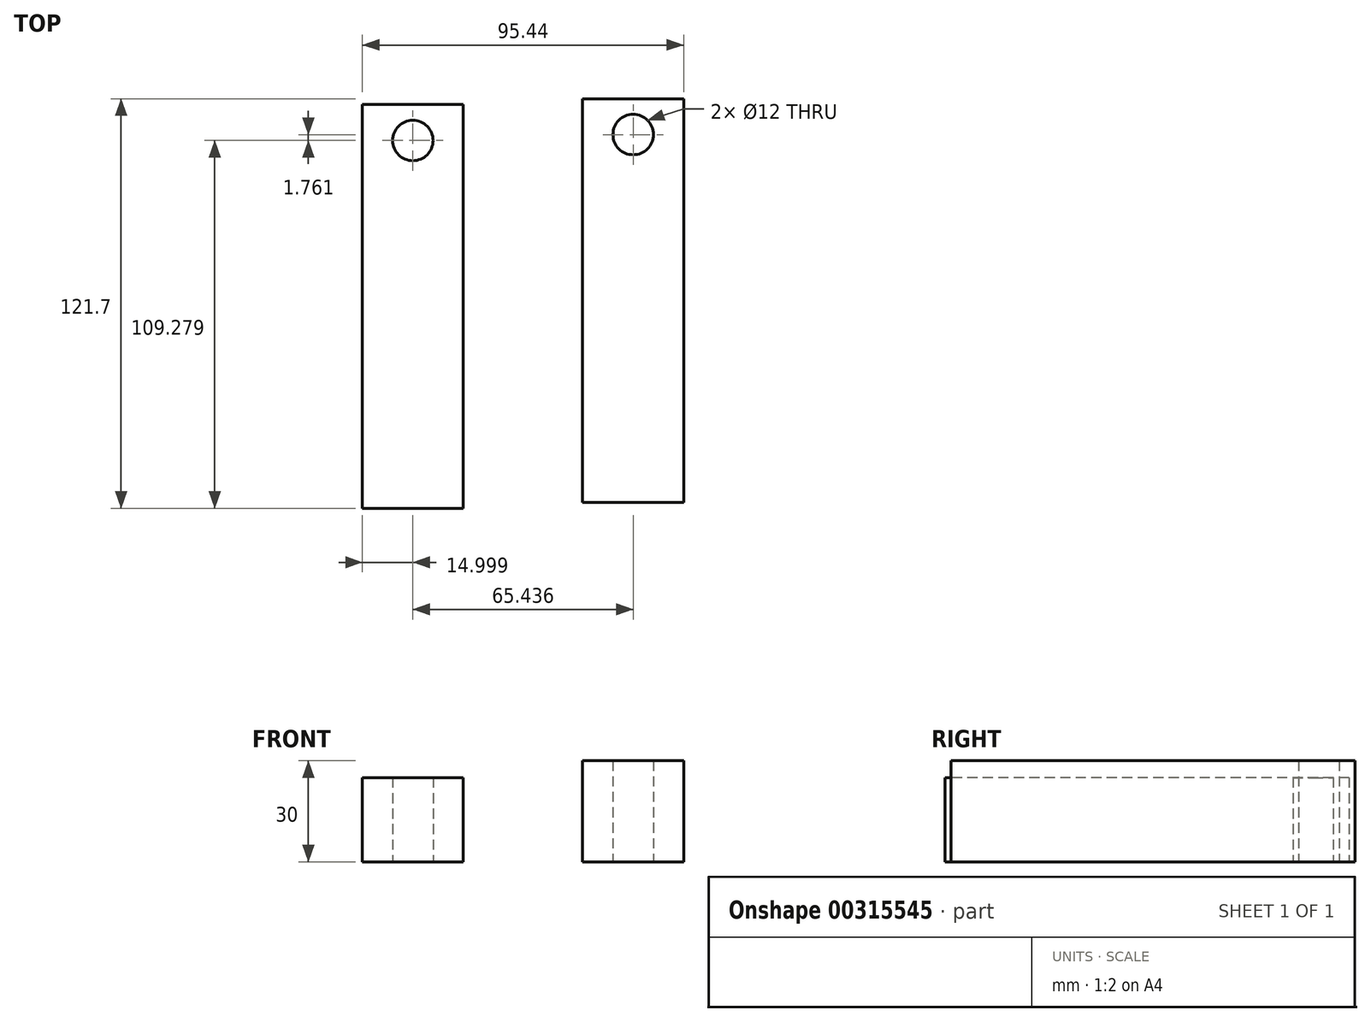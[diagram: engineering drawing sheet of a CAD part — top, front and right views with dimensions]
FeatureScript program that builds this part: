
annotation { "Feature Type Name" : "Feature", "Feature Type Description" : "" }
export const myFeature = defineFeature(function(context is Context, id is Id, definition is map)
    precondition{}
    {
        {
            var Q0;
            Q0=qCreatedBy(makeId("Top.planeOp"),FACE);
            var sketch = newSketch(context, id + "F0", { "sketchPlane" : qUnion([Q0])});
            skLineSegment(sketch, "E0.bottom", {"start": v(-28.07, 58.25) * mm, "end": v(-58.07, 58.25) * mm});
            skLineSegment(sketch, "E0.top", {"start": v(-28.07, -61.75) * mm, "end": v(-58.07, -61.75) * mm});
            skLineSegment(sketch, "E0.left", {"start": v(-28.07, 58.25) * mm, "end": v(-28.07, -61.75) * mm});
            skLineSegment(sketch, "E0.right", {"start": v(-58.07, 58.25) * mm, "end": v(-58.07, -61.75) * mm});
            skLineSegment(sketch, "E1", {"start": v(-43.07, -61.75) * mm, "end": v(-43.07, 58.25) * mm, "construction": true});
            skLineSegment(sketch, "E2", {"start": v(-58.07, 47.53) * mm, "end": v(-28.07, 47.53) * mm, "construction": true});
            skCircle(sketch, "E3", {"center": v(-43.07, 47.53) * mm, "radius": 6 * mm});
            skSolve(sketch);
        }
        {
            var Q0;
            Q0 = qSketchRegion(id + "F0", true);
            extrude(context, id + "F1", {"entities" : qUnion([Q0]), "depth" : 25 * mm});
        }
        {
            var Q0;
            Q0=qCreatedBy(makeId("Top.planeOp"),FACE);
            var sketch = newSketch(context, id + "F2", { "sketchPlane" : qUnion([Q0])});
            skLineSegment(sketch, "E4.bottom", {"start": v(37.37, 59.95) * mm, "end": v(7.37, 59.95) * mm});
            skLineSegment(sketch, "E4.top", {"start": v(37.37, -60.05) * mm, "end": v(7.37, -60.05) * mm});
            skLineSegment(sketch, "E4.left", {"start": v(37.37, 59.95) * mm, "end": v(37.37, -60.05) * mm});
            skLineSegment(sketch, "E4.right", {"start": v(7.37, 59.95) * mm, "end": v(7.37, -60.05) * mm});
            skLineSegment(sketch, "E5", {"start": v(22.37, 59.95) * mm, "end": v(22.37, -60.05) * mm, "construction": true});
            skLineSegment(sketch, "E6", {"start": v(37.37, 49.29) * mm, "end": v(7.37, 49.29) * mm, "construction": true});
            skCircle(sketch, "E7", {"center": v(22.37, 49.29) * mm, "radius": 6 * mm});
            skSolve(sketch);
        }
        {
            var Q0;
            Q0=makeQuery(id+"F2.imprint","IMPRINT",FACE,{"disambiguationData":[TD([[makeQuery(id+"F2.imprint","IMPRINT",EDGE,{"derivedFrom":sQuery(id+"F2.wireOp",EDGE,"E4.bottom")}),1.0]])]});
            var Q1;
            Q1=sQuery(id+"F2.wireOp",EDGE,"E7");
            extrude(context, id + "F3", {"entities" : qUnion([Q0]), "surfaceEntities" : qUnion([Q1]), "depth" : 30 * mm});
        }
    });
